# Revit family: Lighting-UrbanSystem-GEWISS-URBAN[O3]-LED-SIDE_COUPLING_OPTIC_ELLIPTICAL
name_source: partatom
category: Apparecchi per illuminazione
units: mm (PartAtom-declared; Revit-internal decimal feet)

## family parameters
Condiviso = No
Host = Superficie
Numero OmniClass = 23.80.70.00
Punto di calcolo locali = Sì
Quota connettore circolare = Usa diametro
Sorgente d'illuminazione = No
Taglio con vuoti quando caricato = No
Tipo di parte = Normale
Titolo OmniClass = Lighting

## types (4) — shared parameters
Application = External
Catalogue = LIGHTING
Catalogue Range = URBAN [O3]
Colour = Graphite grey
Colour temperature = 4000 K (CRI 70)
Colour temperature: = 4000 K (CRI 70)
Driver type = Constant Current Driver Led
Electrocod = 244C
Finitura = GEWISS - GRIGIO GRAFITE
IDF = 751c2b7a-eeeb-4983-bd51-9f6babd3fdd4
IDT = da31b83e-a88b-4408-9115-206c2dedd00b
IP degree = IP66
Immagine tipo = GWS7251.jpg
Insulation class = II
LED Life time (L80B10) = 100000H
LED Life time (L90B20) = 50000H
LED LifeTime (L80B20) = 50000H
LED current = 530mA
Maximum surface exposed to the wind = 0,25M2
Minimum distance from the illuminated object = 1M
Operating temperature: = -25 +35 °C
Optic = Elliptical - ULOR: 0%
Photobiologic Risk = RG1/RG2 @ 20cm
Pilot current = 530mA
Produttore = GEWISS S.p.A.
Prospetto di default = 1219 mm
Risk photobiological = RG1/RG2 @ 20cm
SEO = Street lighting
Shock resistance = IK08 BODY - IK06 LENS
Suitable for = Commercial side brackets with side connection
Suitable for: = Commercial side brackets with side connection
Technical sheet = https://www.gewiss.com
Type of lamp: = LED
Type of light source = LED
URL = https://www.gewiss.com
Version file RFA = 20.11
Vetro = GEWISS - VETRO
Voltage: = 220/240 V - 50/60 Hz
Warranty = 5 years
Working temperature = -25 +35 °C

## per-type parameters (varying)
| type | Descrizione | EAN code | Lumen output (lm) | Modello | No. Chorus modules | Nominal flux (lm) | Number of modules | Power supply operation | System power | Voltage | Weight (kg) | Weight (kg): |
| GWS7278 - URBAN S.4M LED 4000K BI.P.SIDE B.E.O.GR | URBAN S.4M LED 4000K BI.P.SIDE B.E.O.GR | 8011564803022 | 11240 | GWS7278 | 4 (4x16 LED) | 13400 | 4 (4x16 LED) | Bi power | 105W | 220/240 V - 50/60 Hz - Bi-power with self-learning | 11 | 11 |
| GWS7257 - URBAN SYS.3MOD.LED 4000K SIDE BR.E.O.GR | URBAN SYS.3MOD.LED 4000K SIDE BR.E.O.GR | 8011564802896 | 8590 | GWS7257 | 3 (3x16 LED) | 10230 | 3 (3x16 LED) |  | 81W | 220/240 V - 50/60 Hz - Stand alone and/or possibility of dimmer 1-10 V | 10,3 | 10,3 |
| GWS7258 - URBAN SYS.4MOD.LED 4000K SIDE BR.E.O.GR | URBAN SYS.4MOD.LED 4000K SIDE BR.E.O.GR | 8011564802902 | 11240 | GWS7258 | 4 (4x16 LED) | 13400 | 4 (4x16 LED) |  | 105W | 220/240 V - 50/60 Hz - Stand alone and/or possibility of dimmer 1-10 V | 11 | 11 |
| GWS7277 - URBAN S.3M LED 4000K BI.P.SIDE B.E.O.GR | URBAN S.3M LED 4000K BI.P.SIDE B.E.O.GR | 8011564803015 | 8590 | GWS7277 | 3 (3x16 LED) | 10230 | 3 (3x16 LED) | Bi power | 81W | 220/240 V - 50/60 Hz - Bi-power with self-learning | 10,3 | 10,3 |

## geometry (parser evidence)
native form markers: Blend x4
no freeform markers — native parametric forms only
